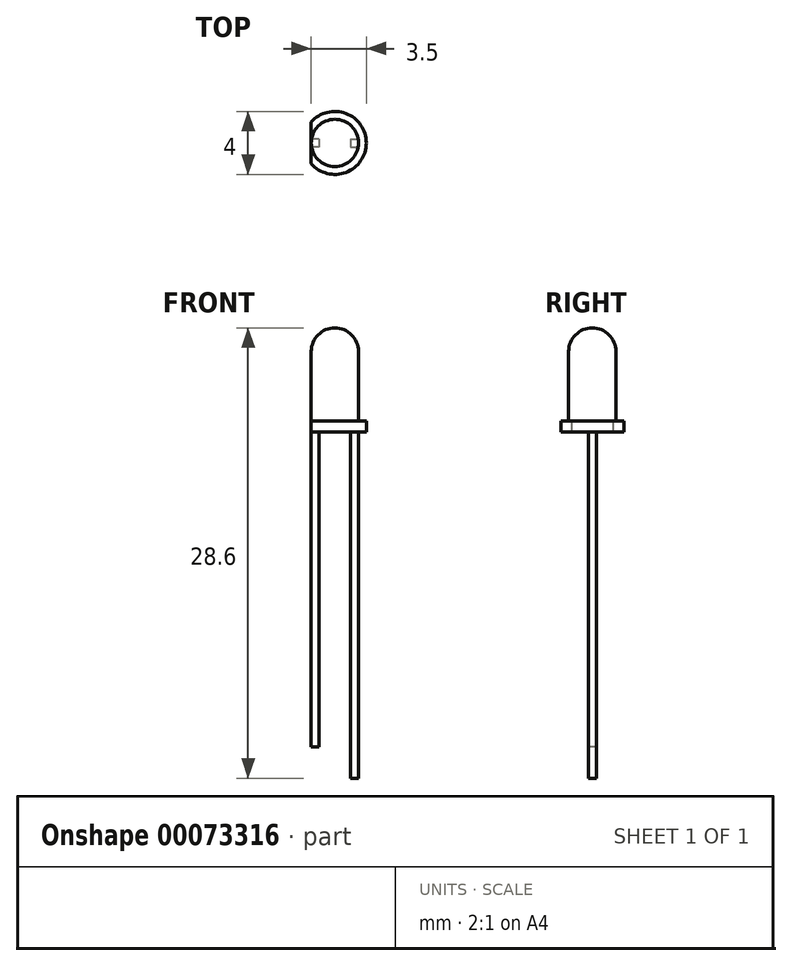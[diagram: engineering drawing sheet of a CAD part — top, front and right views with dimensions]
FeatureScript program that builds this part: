
annotation { "Feature Type Name" : "Feature", "Feature Type Description" : "" }
export const myFeature = defineFeature(function(context is Context, id is Id, definition is map)
    precondition{}
    {
        {
            var Q0;
            Q0=qCreatedBy(makeId("Top.planeOp"),FACE);
            var sketch = newSketch(context, id + "F0", { "sketchPlane" : qUnion([Q0])});
            skCircle(sketch, "E0", {"center": v(0, 0) * mm, "radius": 1.5 * mm});
            skSolve(sketch);
        }
        {
            var Q0;
            Q0=qSketchRegion(id+"F0",true);
            extrude(context, id + "F1", {"entities" : qUnion([Q0]), "depth" : 5.1 * mm});
        }
        {
            var Q0;
            Q0=makeQuery(id+"F1.opExtrude","CAP_FACE",FACE,{"disambiguationData":[OSD([sQuery(id+"F0.wireOp",EDGE,"E0")])],"isStart":false});
            var sketch = newSketch(context, id + "F2", { "sketchPlane" : qUnion([Q0])});
            skLineSegment(sketch, "E1", {"start": v(0, -1.5) * mm, "end": v(0, 1.5) * mm});
            skArc(sketch, "E2", {"start": v(0, 1.5) * mm, "mid": v(-1.5, 0) * mm, "end": v(0, -1.5) * mm});
            skSolve(sketch);
        }
        {
            var Q0;
            Q0=qSketchRegion(id+"F2",true);
            var Q1;
            Q1=sQuery(id+"F2.wireOp",EDGE,"E1");
            revolve(context, id + "F3", {"operationType" : NewBodyOperationType.ADD, "entities" : qUnion([Q0]), "axis" : qUnion([Q1]), "revolveType" : RevolveType.FULL});
        }
        {
            var Q0;
            Q0=makeQuery(id+"F1.opExtrude","CAP_FACE",FACE,{"disambiguationData":[OSD([sQuery(id+"F0.wireOp",EDGE,"E0")])],"isStart":true});
            var sketch = newSketch(context, id + "F4", { "sketchPlane" : qUnion([Q0])});
            skArc(sketch, "E3.0", {"start": v(-1.5, -1.32) * mm, "mid": v(2, 0) * mm, "end": v(-1.5, 1.32) * mm});
            skLineSegment(sketch, "E4", {"start": v(-1.5, -1.32) * mm, "end": v(-1.5, 1.32) * mm});
            skSolve(sketch);
        }
        {
            var Q0;
            Q0=qSketchRegion(id+"F4",true);
            extrude(context, id + "F5", {"entities" : qUnion([Q0]), "operationType" : NewBodyOperationType.ADD, "oppositeDirection" : true, "depth" : .7 * mm});
        }
        {
            var Q0;
            Q0=makeQuery(id+"F5.boolean.opBoolean","MERGE",FACE,{"derivedFrom":[makeQuery(id+"F1.opExtrude","CAP_FACE",FACE,{"disambiguationData":[OSD([sQuery(id+"F0.wireOp",EDGE,"E0")])],"isStart":true}),makeQuery(id+"F5.opExtrude","CAP_FACE",FACE,{"disambiguationData":[OSD([sQuery(id+"F4.wireOp",EDGE,"E3.0"),sQuery(id+"F4.wireOp",EDGE,"E4")])],"isStart":true})]});
            var sketch = newSketch(context, id + "F6", { "sketchPlane" : qUnion([Q0])});
            skLineSegment(sketch, "E5.rect.bottom", {"start": v(1, -0.25) * mm, "end": v(1.5, -0.25) * mm});
            skLineSegment(sketch, "E5.rect.top", {"start": v(1, 0.25) * mm, "end": v(1.5, 0.25) * mm});
            skLineSegment(sketch, "E5.rect.left", {"start": v(1, -0.25) * mm, "end": v(1, 0.25) * mm});
            skLineSegment(sketch, "E5.rect.right", {"start": v(1.5, -0.25) * mm, "end": v(1.5, 0.25) * mm});
            skPoint(sketch, "E5.rect.middle", {"position": v(1.25, 0) * mm});
            skLineSegment(sketch, "E6.rect.bottom", {"start": v(-1, -0.25) * mm, "end": v(-1.5, -0.25) * mm});
            skLineSegment(sketch, "E6.rect.top", {"start": v(-1, 0.25) * mm, "end": v(-1.5, 0.25) * mm});
            skLineSegment(sketch, "E6.rect.left", {"start": v(-1, -0.25) * mm, "end": v(-1, 0.25) * mm});
            skLineSegment(sketch, "E6.rect.right", {"start": v(-1.5, -0.25) * mm, "end": v(-1.5, 0.25) * mm});
            skPoint(sketch, "E6.rect.middle", {"position": v(-1.25, 0) * mm});
            skLineSegment(sketch, "E7", {"start": v(1.5, -0.25) * mm, "end": v(1, 0.25) * mm, "construction": true});
            skLineSegment(sketch, "E8", {"start": v(1.5, 0.25) * mm, "end": v(1, -0.25) * mm, "construction": true});
            skLineSegment(sketch, "E9", {"start": v(-1, -0.25) * mm, "end": v(-1.5, 0.25) * mm, "construction": true});
            skLineSegment(sketch, "E10", {"start": v(-1, 0.25) * mm, "end": v(-1.5, -0.25) * mm, "construction": true});
            skLineSegment(sketch, "E11", {"start": v(1.25, 0) * mm, "end": v(-1.25, 0) * mm, "construction": true});
            skSolve(sketch);
        }
        {
            var Q0;
            Q0=qSketchRegion(id+"F6",true);
            extrude(context, id + "F7", {"entities" : qUnion([Q0]), "operationType" : NewBodyOperationType.ADD, "depth" : 20 * mm});
        }
        {
            var Q0;
            Q0=makeQuery(id+"F7.opExtrude","CAP_FACE",FACE,{"disambiguationData":[OSD([sQuery(id+"F6.wireOp",EDGE,"E5.rect.bottom"),sQuery(id+"F6.wireOp",EDGE,"E5.rect.top"),sQuery(id+"F6.wireOp",EDGE,"E5.rect.left"),sQuery(id+"F6.wireOp",EDGE,"E5.rect.right")])],"isStart":false});
            extrude(context, id + "F8", {"entities" : qUnion([Q0]), "operationType" : NewBodyOperationType.ADD, "depth" : 2 * mm});
        }
    });
